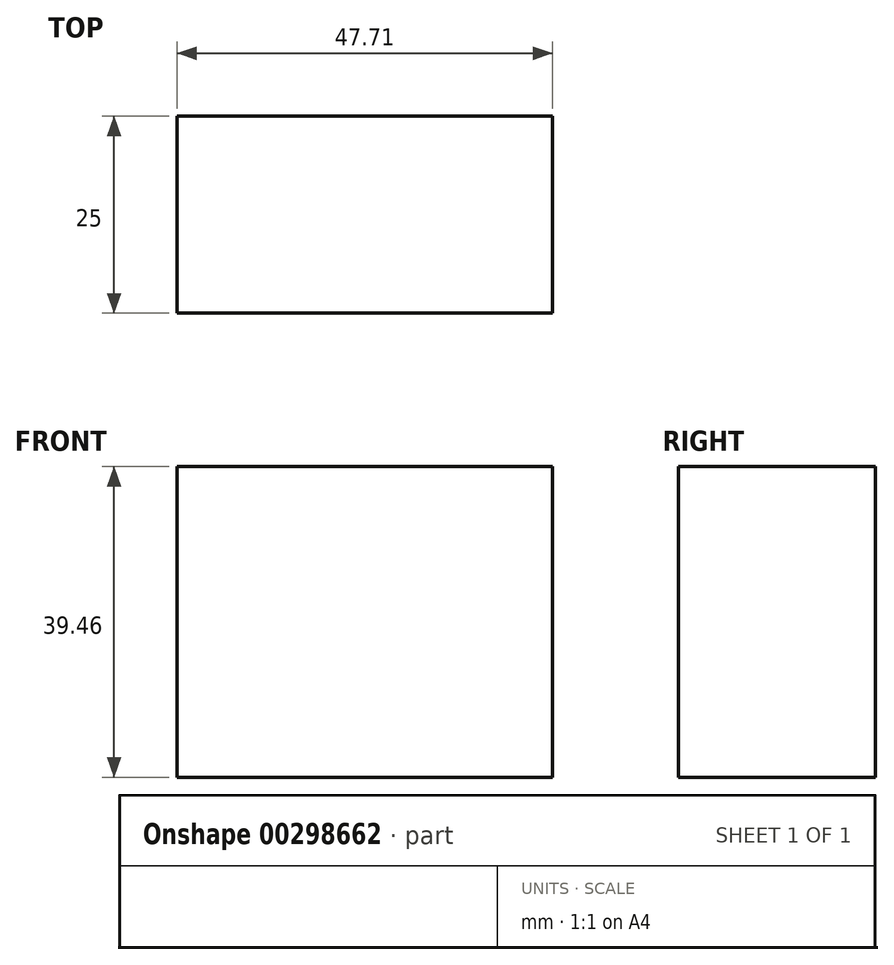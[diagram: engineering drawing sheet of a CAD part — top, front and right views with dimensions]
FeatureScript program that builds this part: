
annotation { "Feature Type Name" : "Feature", "Feature Type Description" : "" }
export const myFeature = defineFeature(function(context is Context, id is Id, definition is map)
    precondition{}
    {
        {
            var Q0;
            Q0=qCreatedBy(makeId("Front.planeOp"),FACE);
            var sketch = newSketch(context, id + "F0", { "sketchPlane" : qUnion([Q0])});
            skLineSegment(sketch, "E0.bottom", {"start": v(-116.84, 67.2) * mm, "end": v(-69.13, 67.2) * mm});
            skLineSegment(sketch, "E0.top", {"start": v(-116.84, 27.75) * mm, "end": v(-69.13, 27.75) * mm});
            skLineSegment(sketch, "E0.left", {"start": v(-116.84, 67.2) * mm, "end": v(-116.84, 27.75) * mm});
            skLineSegment(sketch, "E0.right", {"start": v(-69.13, 67.2) * mm, "end": v(-69.13, 27.75) * mm});
            skSolve(sketch);
        }
        {
            var Q0;
            Q0 = qSketchRegion(id + "F0", true);
            extrude(context, id + "F1", {"entities" : qUnion([Q0]), "depth" : 25 * mm});
        }
    });
